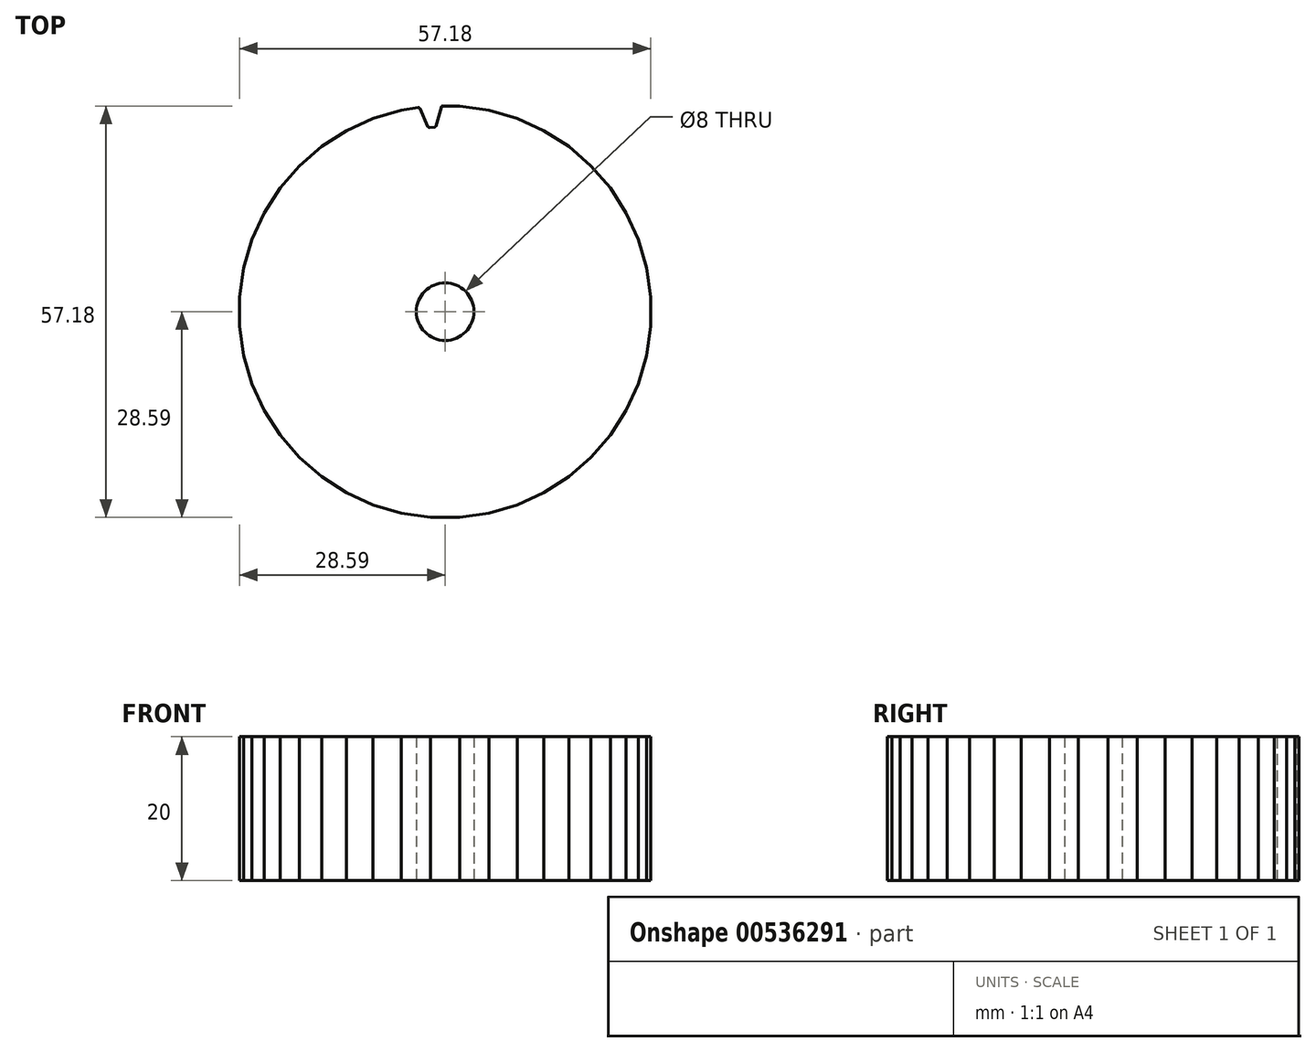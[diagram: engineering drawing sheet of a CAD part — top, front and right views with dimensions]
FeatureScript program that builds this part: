
annotation { "Feature Type Name" : "Feature", "Feature Type Description" : "" }
export const myFeature = defineFeature(function(context is Context, id is Id, definition is map)
    precondition{}
    {
        {
            var Q0;
            Q0=qCreatedBy(makeId("Top.planeOp"),FACE);
            var sketch = newSketch(context, id + "F0", { "sketchPlane" : qUnion([Q0])});
            skCircle(sketch, "E0.cCircle", {"center": v(0, 0) * mm, "radius": 28.6 * mm, "construction": true});
            skLineSegment(sketch, "E0.0", {"start": v(28.6, 2.05) * mm, "end": v(28.6, -2.05) * mm});
            skLineSegment(sketch, "E0.1", {"start": v(28.6, -2.05) * mm, "end": v(28.01, -6.1) * mm});
            skLineSegment(sketch, "E0.2", {"start": v(28.01, -6.1) * mm, "end": v(26.86, -10.02) * mm});
            skLineSegment(sketch, "E0.3", {"start": v(26.86, -10.02) * mm, "end": v(25.16, -13.74) * mm});
            skLineSegment(sketch, "E0.4", {"start": v(25.16, -13.74) * mm, "end": v(22.95, -17.18) * mm});
            skLineSegment(sketch, "E0.5", {"start": v(22.95, -17.18) * mm, "end": v(20.27, -20.27) * mm});
            skLineSegment(sketch, "E0.6", {"start": v(20.27, -20.27) * mm, "end": v(17.18, -22.95) * mm});
            skLineSegment(sketch, "E0.7", {"start": v(17.18, -22.95) * mm, "end": v(13.74, -25.16) * mm});
            skLineSegment(sketch, "E0.8", {"start": v(13.74, -25.16) * mm, "end": v(10.02, -26.86) * mm});
            skLineSegment(sketch, "E0.9", {"start": v(10.02, -26.86) * mm, "end": v(6.1, -28.01) * mm});
            skLineSegment(sketch, "E0.10", {"start": v(6.1, -28.01) * mm, "end": v(2.05, -28.6) * mm});
            skLineSegment(sketch, "E0.11", {"start": v(2.05, -28.6) * mm, "end": v(-2.05, -28.6) * mm});
            skLineSegment(sketch, "E0.12", {"start": v(-2.05, -28.6) * mm, "end": v(-6.1, -28.01) * mm});
            skLineSegment(sketch, "E0.13", {"start": v(-6.1, -28.01) * mm, "end": v(-10.02, -26.86) * mm});
            skLineSegment(sketch, "E0.14", {"start": v(-10.02, -26.86) * mm, "end": v(-13.74, -25.16) * mm});
            skLineSegment(sketch, "E0.15", {"start": v(-13.74, -25.16) * mm, "end": v(-17.18, -22.95) * mm});
            skLineSegment(sketch, "E0.16", {"start": v(-17.18, -22.95) * mm, "end": v(-20.27, -20.27) * mm});
            skLineSegment(sketch, "E0.17", {"start": v(-20.27, -20.27) * mm, "end": v(-22.95, -17.18) * mm});
            skLineSegment(sketch, "E0.18", {"start": v(-22.95, -17.18) * mm, "end": v(-25.16, -13.74) * mm});
            skLineSegment(sketch, "E0.19", {"start": v(-25.16, -13.74) * mm, "end": v(-26.86, -10.02) * mm});
            skLineSegment(sketch, "E0.20", {"start": v(-26.86, -10.02) * mm, "end": v(-28.01, -6.1) * mm});
            skLineSegment(sketch, "E0.21", {"start": v(-28.01, -6.1) * mm, "end": v(-28.6, -2.05) * mm});
            skLineSegment(sketch, "E0.22", {"start": v(-28.6, -2.05) * mm, "end": v(-28.6, 2.05) * mm});
            skLineSegment(sketch, "E0.23", {"start": v(-28.6, 2.05) * mm, "end": v(-28.01, 6.1) * mm});
            skLineSegment(sketch, "E0.24", {"start": v(-28.01, 6.1) * mm, "end": v(-26.86, 10.02) * mm});
            skLineSegment(sketch, "E0.25", {"start": v(-26.86, 10.02) * mm, "end": v(-25.16, 13.74) * mm});
            skLineSegment(sketch, "E0.26", {"start": v(-25.16, 13.74) * mm, "end": v(-22.95, 17.18) * mm});
            skLineSegment(sketch, "E0.27", {"start": v(-22.95, 17.18) * mm, "end": v(-20.27, 20.27) * mm});
            skLineSegment(sketch, "E0.28", {"start": v(-20.27, 20.27) * mm, "end": v(-17.18, 22.95) * mm});
            skLineSegment(sketch, "E0.29", {"start": v(-17.18, 22.95) * mm, "end": v(-13.74, 25.16) * mm});
            skLineSegment(sketch, "E0.30", {"start": v(-13.74, 25.16) * mm, "end": v(-10.02, 26.86) * mm});
            skLineSegment(sketch, "E0.31", {"start": v(-10.02, 26.86) * mm, "end": v(-6.1, 28.01) * mm});
            skLineSegment(sketch, "E0.32", {"start": v(-6.1, 28.01) * mm, "end": v(-2.05, 28.6) * mm});
            skLineSegment(sketch, "E0.33", {"start": v(-2.05, 28.6) * mm, "end": v(2.05, 28.6) * mm});
            skLineSegment(sketch, "E0.34", {"start": v(2.05, 28.6) * mm, "end": v(6.1, 28.01) * mm});
            skLineSegment(sketch, "E0.35", {"start": v(6.1, 28.01) * mm, "end": v(10.02, 26.86) * mm});
            skLineSegment(sketch, "E0.36", {"start": v(10.02, 26.86) * mm, "end": v(13.74, 25.16) * mm});
            skLineSegment(sketch, "E0.37", {"start": v(13.74, 25.16) * mm, "end": v(17.18, 22.95) * mm});
            skLineSegment(sketch, "E0.38", {"start": v(17.18, 22.95) * mm, "end": v(20.27, 20.27) * mm});
            skLineSegment(sketch, "E0.39", {"start": v(20.27, 20.27) * mm, "end": v(22.95, 17.18) * mm});
            skLineSegment(sketch, "E0.40", {"start": v(22.95, 17.18) * mm, "end": v(25.16, 13.74) * mm});
            skLineSegment(sketch, "E0.41", {"start": v(25.16, 13.74) * mm, "end": v(26.86, 10.02) * mm});
            skLineSegment(sketch, "E0.42", {"start": v(26.86, 10.02) * mm, "end": v(28.01, 6.1) * mm});
            skLineSegment(sketch, "E0.43", {"start": v(28.01, 6.1) * mm, "end": v(28.6, 2.05) * mm});
            skPoint(sketch, "E0.0.midPoint", {"position": v(28.6, 0) * mm});
            skCircle(sketch, "E1", {"center": v(0, 0) * mm, "radius": 4 * mm});
            skSolve(sketch);
        }
        {
            var Q0;
            Q0=makeQuery(id+"F0.imprint","IMPRINT",FACE,{"disambiguationData":[TD([[makeQuery(id+"F0.imprint","IMPRINT",EDGE,{"derivedFrom":sQuery(id+"F0.wireOp",EDGE,"E0.0")}),-1.0]])]});
            extrude(context, id + "F1", {"entities" : qUnion([Q0]), "depth" : 20 * mm, "offsetDistance" : 25 * mm});
        }
        {
            var Q0;
            Q0=makeQuery(id+"F1.opExtrude","CAP_FACE",FACE,{"disambiguationData":[OSD([sQuery(id+"F0.wireOp",EDGE,"E0.0"),sQuery(id+"F0.wireOp",EDGE,"E0.1"),sQuery(id+"F0.wireOp",EDGE,"E0.2"),sQuery(id+"F0.wireOp",EDGE,"E0.3"),sQuery(id+"F0.wireOp",EDGE,"E0.4"),sQuery(id+"F0.wireOp",EDGE,"E0.5"),sQuery(id+"F0.wireOp",EDGE,"E0.6"),sQuery(id+"F0.wireOp",EDGE,"E0.7"),sQuery(id+"F0.wireOp",EDGE,"E0.8"),sQuery(id+"F0.wireOp",EDGE,"E0.9"),sQuery(id+"F0.wireOp",EDGE,"E0.10"),sQuery(id+"F0.wireOp",EDGE,"E0.11"),sQuery(id+"F0.wireOp",EDGE,"E0.12"),sQuery(id+"F0.wireOp",EDGE,"E0.13"),sQuery(id+"F0.wireOp",EDGE,"E0.14"),sQuery(id+"F0.wireOp",EDGE,"E0.15"),sQuery(id+"F0.wireOp",EDGE,"E0.16"),sQuery(id+"F0.wireOp",EDGE,"E0.17"),sQuery(id+"F0.wireOp",EDGE,"E0.18"),sQuery(id+"F0.wireOp",EDGE,"E0.19"),sQuery(id+"F0.wireOp",EDGE,"E0.20"),sQuery(id+"F0.wireOp",EDGE,"E0.21"),sQuery(id+"F0.wireOp",EDGE,"E0.22"),sQuery(id+"F0.wireOp",EDGE,"E0.23"),sQuery(id+"F0.wireOp",EDGE,"E0.24"),sQuery(id+"F0.wireOp",EDGE,"E0.25"),sQuery(id+"F0.wireOp",EDGE,"E0.26"),sQuery(id+"F0.wireOp",EDGE,"E0.27"),sQuery(id+"F0.wireOp",EDGE,"E0.28"),sQuery(id+"F0.wireOp",EDGE,"E0.29"),sQuery(id+"F0.wireOp",EDGE,"E0.30"),sQuery(id+"F0.wireOp",EDGE,"E0.31"),sQuery(id+"F0.wireOp",EDGE,"E0.32"),sQuery(id+"F0.wireOp",EDGE,"E0.33"),sQuery(id+"F0.wireOp",EDGE,"E0.34"),sQuery(id+"F0.wireOp",EDGE,"E0.35"),sQuery(id+"F0.wireOp",EDGE,"E0.36"),sQuery(id+"F0.wireOp",EDGE,"E0.37"),sQuery(id+"F0.wireOp",EDGE,"E0.38"),sQuery(id+"F0.wireOp",EDGE,"E0.39"),sQuery(id+"F0.wireOp",EDGE,"E0.40"),sQuery(id+"F0.wireOp",EDGE,"E0.41"),sQuery(id+"F0.wireOp",EDGE,"E0.42"),sQuery(id+"F0.wireOp",EDGE,"E0.43"),sQuery(id+"F0.wireOp",EDGE,"E1")])],"isStart":false});
            var sketch = newSketch(context, id + "F2", { "sketchPlane" : qUnion([Q0])});
            skLineSegment(sketch, "E2", {"start": v(-3.51, 28.24) * mm, "end": v(-2.39, 25.72) * mm});
            skLineSegment(sketch, "E3", {"start": v(-2.2, 25.6) * mm, "end": v(-1.47, 25.66) * mm});
            skLineSegment(sketch, "E4", {"start": v(-1.3, 25.8) * mm, "end": v(-0.54, 28.45) * mm});
            skLineSegment(sketch, "E5", {"start": v(-3.57, 28.37) * mm, "end": v(-2.05, 28.6) * mm});
            skLineSegment(sketch, "E6", {"start": v(-2.05, 28.6) * mm, "end": v(-0.5, 28.6) * mm});
            skLineSegment(sketch, "E7", {"start": v(-3.72, 28.35) * mm, "end": v(-4.07, 28.3) * mm});
            skLineSegment(sketch, "E8", {"start": v(-0.35, 28.6) * mm, "end": v(0, 28.6) * mm});
            skPoint(sketch, "E9.visualSharp", {"position": v(-3.57, 28.37) * mm});
            skArc(sketch, "E9.filletArc", {"start": v(-3.51, 28.24) * mm, "mid": v(-3.6, 28.33) * mm, "end": v(-3.72, 28.35) * mm});
            skPoint(sketch, "E10.visualSharp", {"position": v(-0.5, 28.6) * mm});
            skArc(sketch, "E10.filletArc", {"start": v(-0.35, 28.6) * mm, "mid": v(-0.47, 28.55) * mm, "end": v(-0.54, 28.45) * mm});
            skPoint(sketch, "E11.visualSharp", {"position": v(-2.33, 25.6) * mm});
            skArc(sketch, "E11.filletArc", {"start": v(-2.39, 25.72) * mm, "mid": v(-2.3, 25.63) * mm, "end": v(-2.2, 25.6) * mm});
            skPoint(sketch, "E12.visualSharp", {"position": v(-1.33, 25.67) * mm});
            skArc(sketch, "E12.filletArc", {"start": v(-1.47, 25.66) * mm, "mid": v(-1.36, 25.7) * mm, "end": v(-1.3, 25.8) * mm});
            skSolve(sketch);
        }
        {
            var Q0;
            Q0=makeQuery(id+"F2.imprint","IMPRINT",FACE,{"disambiguationData":[TD([[makeQuery(id+"F2.imprint","IMPRINT",EDGE,{"derivedFrom":sQuery(id+"F2.wireOp",EDGE,"E2")}),1.0]])]});
            extrude(context, id + "F3", {"entities" : qUnion([Q0]), "operationType" : NewBodyOperationType.REMOVE, "endBound" : BoundingType.THROUGH_ALL, "oppositeDirection" : true, "depth" : 25 * mm, "offsetDistance" : 25 * mm});
        }
        {
            var Q0;
            Q0=qCreatedBy(makeId("Front.planeOp"),FACE);
            var sketch = newSketch(context, id + "F4", { "sketchPlane" : qUnion([Q0])});
            skLineSegment(sketch, "E13", {"start": v(0, 0) * mm, "end": v(0, 63.61) * mm});
            skLineSegment(sketch, "E14", {"start": v(0, 63.61) * mm, "end": v(0, -63.87) * mm});
            skSolve(sketch);
        }
    });
